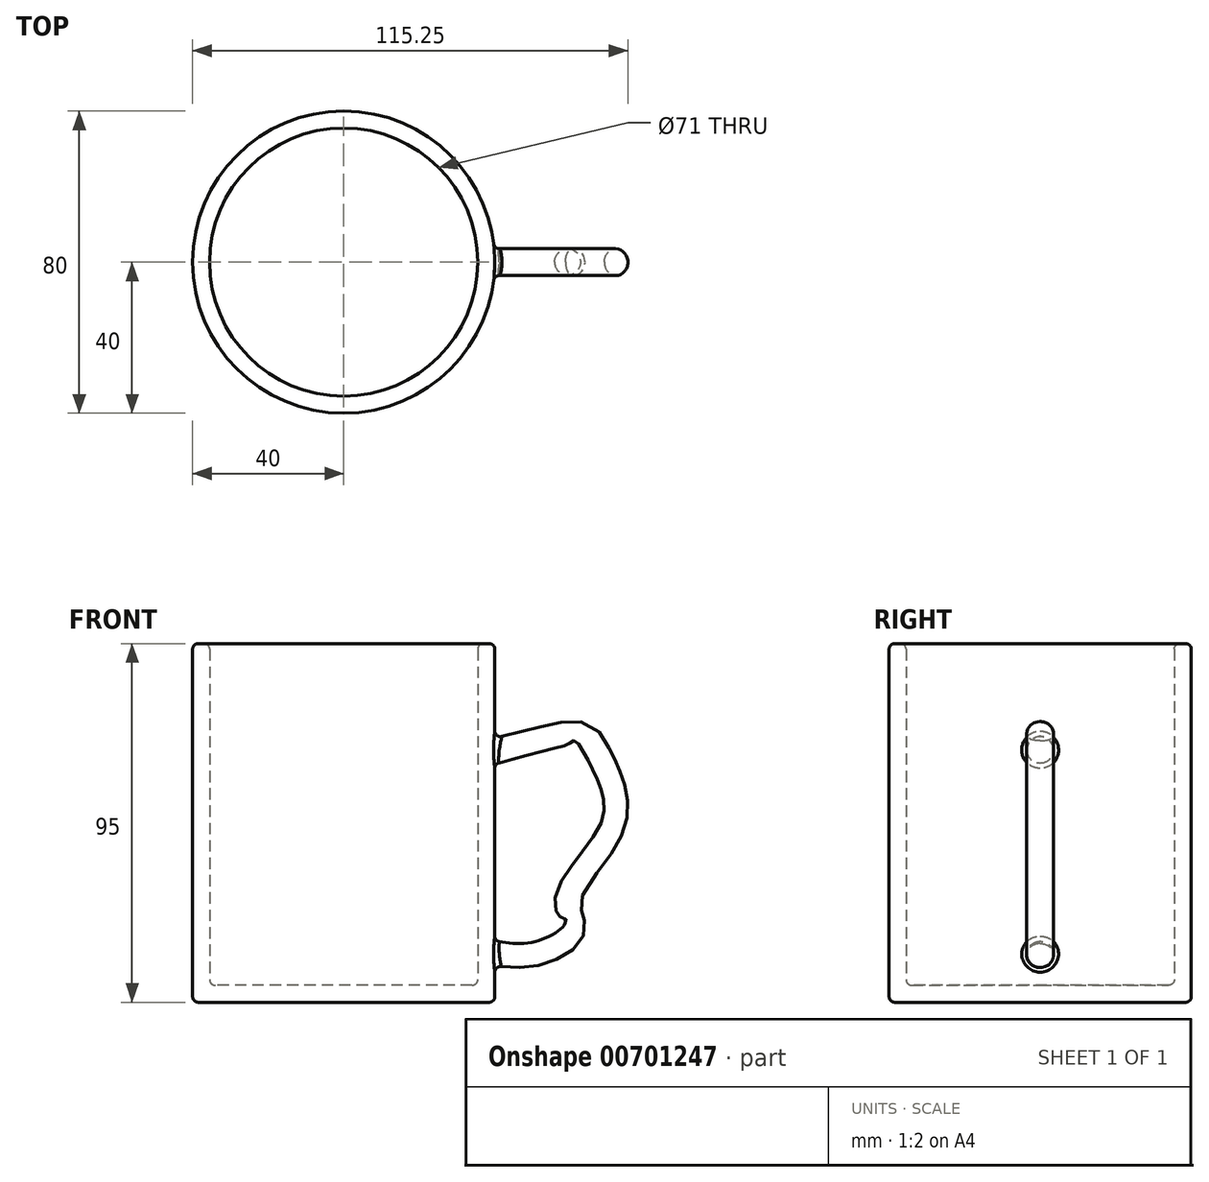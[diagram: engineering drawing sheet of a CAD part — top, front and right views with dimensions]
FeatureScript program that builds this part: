
annotation { "Feature Type Name" : "Feature", "Feature Type Description" : "" }
export const myFeature = defineFeature(function(context is Context, id is Id, definition is map)
    precondition{}
    {
        {
            var Q0;
            Q0=qCreatedBy(makeId("Top.planeOp"),FACE);
            var sketch = newSketch(context, id + "F0", { "sketchPlane" : qUnion([Q0])});
            skCircle(sketch, "E0", {"center": v(0, 0) * mm, "radius": 40 * mm});
            skSolve(sketch);
        }
        {
            var Q0;
            Q0=makeQuery(id+"F0.imprint","IMPRINT",FACE,{"disambiguationData":[TD([[makeQuery(id+"F0.imprint","IMPRINT",EDGE,{"derivedFrom":sQuery(id+"F0.wireOp",EDGE,"E0")}),1.0]])]});
            extrude(context, id + "F1", {"entities" : qUnion([Q0]), "depth" : 95 * mm, "offsetDistance" : 25 * mm});
        }
        {
            var Q0;
            Q0=qCreatedBy(makeId("Front.planeOp"),FACE);
            var sketch = newSketch(context, id + "F2", { "sketchPlane" : qUnion([Q0])});
            skFitSpline(sketch, "E1", {"points": [v(32.87, 64.13) * mm, v(49.11, 69.2) * mm, v(63.23, 71.08) * mm, v(66.9, 67.3) * mm, v(70.76, 59.15) * mm, v(71.04, 45.68) * mm, v(59.78, 27.14) * mm, v(60.81, 19.05) * mm, v(48.25, 12.24) * mm, v(34.19, 14.37) * mm, v(32.7, 15) * mm], "startDerivative": vector(136.82, 59.28) * mm, "endDerivative": vector(-30.1, 14.88) * mm});
            skSolve(sketch);
        }
        {
            var Q0;
            Q0=qCreatedBy(makeId("Right.planeOp"),FACE);
            cPlane(context, id + "F3", {"entities" : qUnion([Q0]), "cplaneType" : CPlaneType.OFFSET, "offset" : 31.9 * mm, "width" : 150 * mm, "height" : 150 * mm});
        }
        {
            var Q0;
            Q0=qCreatedBy(id+"F3.planeOp",FACE);
            var sketch = newSketch(context, id + "F4", { "sketchPlane" : qUnion([Q0])});
            skCircle(sketch, "E2", {"center": v(0, 63.39) * mm, "radius": 3.56 * mm});
            skSolve(sketch);
        }
        {
            var Q0;
            Q0 = qSketchRegion(id + "F4", true);
            var Q1;
            Q1=sQuery(id+"F2.wireOp",EDGE,"E1");
            sweep(context, id + "F5", {"operationType" : NewBodyOperationType.ADD, "profiles" : qUnion([Q0]), "path" : qUnion([Q1])});
        }
        {
            var Q0;
            Q0=makeQuery(id+"F1.opExtrude","CAP_FACE",FACE,{"disambiguationData":[OSD([sQuery(id+"F0.wireOp",EDGE,"E0")])],"isStart":false});
            shell(context, id + "F6", {"entities" : qUnion([Q0]), "thickness" : 4.5 * mm});
        }
        {
            var Q0;
            Q0=makeQuery(id+"F1.opExtrude","CAP_EDGE",EDGE,{"disambiguationData":[OSD([sQuery(id+"F0.wireOp",EDGE,"E0")])],"isStart":false});
            var Q1;
            {var subQ0=sQuery(id+"F0.wireOp",EDGE,"E0");Q1=makeQuery(id+"F6.opShell","OFFSET_EDGE",EDGE,{"disambiguationData":[OSD([subQ0]),TDD([makeQuery(id+"F1.opExtrude","CAP_EDGE",EDGE,{"disambiguationData":[OSD([subQ0])],"isStart":false})])]});}
            var Q2;
            {var subQ0=sQuery(id+"F0.wireOp",EDGE,"E0");Q2=makeQuery(id+"F6.opShell","OFFSET_FACE",FACE,{"disambiguationData":[OSD([subQ0]),TDD([makeQuery(id+"F1.opExtrude","CAP_FACE",FACE,{"disambiguationData":[OSD([subQ0])],"isStart":true})])]});}
            var Q3;
            Q3=makeQuery(id+"F5.boolean.opBoolean","INTERSECT",EDGE,{"disambiguationData":[OD(1.0)],"derivedFrom":[makeQuery(id+"F1.opExtrude","SWEPT_FACE",FACE,{"disambiguationData":[OSD([sQuery(id+"F0.wireOp",EDGE,"E0")])]}),makeQuery(id+"F5.opSweep","SWEPT_FACE",FACE,{"disambiguationData":[OSD([sQuery(id+"F2.wireOp",EDGE,"E1"),sQuery(id+"F4.wireOp",EDGE,"E2")])]})]});
            var Q4;
            Q4=makeQuery(id+"F5.boolean.opBoolean","INTERSECT",EDGE,{"disambiguationData":[OD(0.0)],"derivedFrom":[makeQuery(id+"F1.opExtrude","SWEPT_FACE",FACE,{"disambiguationData":[OSD([sQuery(id+"F0.wireOp",EDGE,"E0")])]}),makeQuery(id+"F5.opSweep","SWEPT_FACE",FACE,{"disambiguationData":[OSD([sQuery(id+"F2.wireOp",EDGE,"E1"),sQuery(id+"F4.wireOp",EDGE,"E2")])]})]});
            var Q5;
            Q5=makeQuery(id+"F1.opExtrude","CAP_EDGE",EDGE,{"disambiguationData":[OSD([sQuery(id+"F0.wireOp",EDGE,"E0")])],"isStart":true});
            fillet(context, id + "F7", {"entities" : qUnion([Q0, Q1, Q2, Q3, Q4, Q5]), "radius" : 1.5 * mm, "tangentPropagation" : true, "allowEdgeOverflow" : false});
        }
    });
